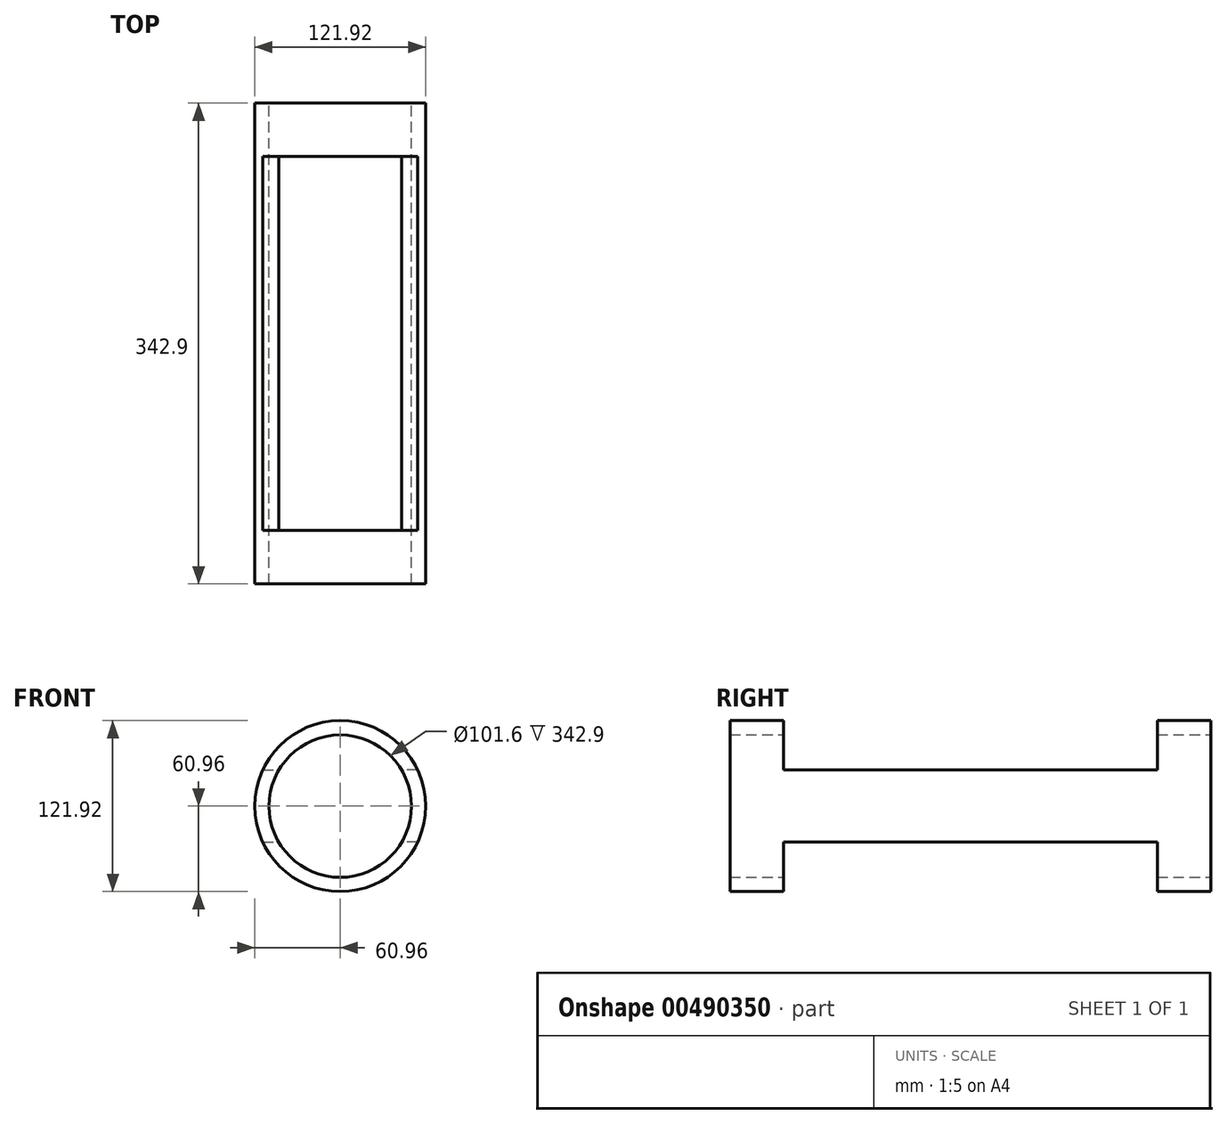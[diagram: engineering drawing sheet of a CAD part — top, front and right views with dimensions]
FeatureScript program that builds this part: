
annotation { "Feature Type Name" : "Feature", "Feature Type Description" : "" }
export const myFeature = defineFeature(function(context is Context, id is Id, definition is map)
    precondition{}
    {
        {
            var Q0;
            Q0=qCreatedBy(makeId("Front.planeOp"),FACE);
            var sketch = newSketch(context, id + "F0", { "sketchPlane" : qUnion([Q0])});
            skCircle(sketch, "E0", {"center": v(0, 0) * mm, "radius": 60.96 * mm});
            skCircle(sketch, "E1", {"center": v(0, 0) * mm, "radius": 50.8 * mm});
            skLineSegment(sketch, "E2", {"start": v(-55.27, -25.72) * mm, "end": v(-43.8, -25.72) * mm});
            skLineSegment(sketch, "E3", {"start": v(-55.27, 25.72) * mm, "end": v(-43.8, 25.72) * mm});
            skLineSegment(sketch, "E4", {"start": v(55.27, -25.72) * mm, "end": v(43.8, -25.72) * mm});
            skLineSegment(sketch, "E5", {"start": v(55.27, 25.72) * mm, "end": v(43.8, 25.72) * mm});
            skSolve(sketch);
        }
        {
            var Q0;
            {var subQ0=sQuery(id+"F0.wireOp",EDGE,"E2");Q0=makeQuery(id+"F0.imprint","IMPRINT",FACE,{"disambiguationData":[TD([[makeQuery(id+"F0.imprint","IMPRINT",EDGE,{"derivedFrom":subQ0}),1.0]])]});}
            var Q1;
            {var subQ0=sQuery(id+"F0.wireOp",EDGE,"E4");Q1=makeQuery(id+"F0.imprint","IMPRINT",FACE,{"disambiguationData":[TD([[makeQuery(id+"F0.imprint","IMPRINT",EDGE,{"derivedFrom":subQ0}),-1.0]])]});}
            extrude(context, id + "F1", {"entities" : qUnion([Q0, Q1]), "depth" : 304.8 * mm});
        }
        {
            var Q0;
            {var subQ0=sQuery(id+"F0.wireOp",EDGE,"E3");Q0=makeQuery(id+"F0.imprint","IMPRINT",FACE,{"disambiguationData":[TD([[makeQuery(id+"F0.imprint","IMPRINT",EDGE,{"derivedFrom":subQ0}),1.0]])]});}
            var Q1;
            {var subQ0=sQuery(id+"F0.wireOp",EDGE,"E2");Q1=makeQuery(id+"F0.imprint","IMPRINT",FACE,{"disambiguationData":[TD([[makeQuery(id+"F0.imprint","IMPRINT",EDGE,{"derivedFrom":subQ0}),-1.0]])]});}
            extrude(context, id + "F2", {"entities" : qUnion([Q0, Q1]), "operationType" : NewBodyOperationType.ADD, "depth" : 38.1 * mm});
        }
        {
            var Q0;
            Q0=makeQuery(id+"F1.opExtrude","CAP_FACE",FACE,{"disambiguationData":[OSD([sQuery(id+"F0.wireOp",EDGE,"E0"),sQuery(id+"F0.wireOp",EDGE,"E1"),sQuery(id+"F0.wireOp",EDGE,"E2"),sQuery(id+"F0.wireOp",EDGE,"E3")])],"isStart":false});
            var sketch = newSketch(context, id + "F3", { "sketchPlane" : qUnion([Q0])});
            skCircle(sketch, "E6", {"center": v(0, 0) * mm, "radius": 60.96 * mm});
            skCircle(sketch, "E7", {"center": v(0, 0) * mm, "radius": 50.8 * mm});
            skSolve(sketch);
        }
        {
            var Q0;
            {var subQ0=sQuery(id+"F3.wireOp",EDGE,"E6");var subQ1=makeQuery(id+"F1.opExtrude","CAP_EDGE",EDGE,{"disambiguationData":[OSD([sQuery(id+"F0.wireOp",EDGE,"E2")])],"isStart":false});var subQ2=makeQuery(id+"F3.imprint","INTERSECT",VERTEX,{"derivedFrom":[subQ1,subQ0]});Q0=makeQuery(id+"F3.imprint","IMPRINT",FACE,{"disambiguationData":[TD([[makeQuery(id+"F3.imprint","IMPRINT",EDGE,{"disambiguationData":[TD([[subQ2,-1.0]])],"derivedFrom":subQ0}),1.0]])]});}
            var Q1;
            {var subQ0=sQuery(id+"F3.wireOp",EDGE,"E6");var subQ1=makeQuery(id+"F1.opExtrude","CAP_EDGE",EDGE,{"disambiguationData":[OSD([sQuery(id+"F0.wireOp",EDGE,"E2")])],"isStart":false});var subQ2=makeQuery(id+"F3.imprint","INTERSECT",VERTEX,{"derivedFrom":[subQ1,subQ0]});Q1=makeQuery(id+"F3.imprint","IMPRINT",FACE,{"disambiguationData":[TD([[makeQuery(id+"F3.imprint","IMPRINT",EDGE,{"disambiguationData":[TD([[subQ2,1.0]])],"derivedFrom":subQ0}),1.0]])]});}
            extrude(context, id + "F4", {"entities" : qUnion([Q0, Q1]), "operationType" : NewBodyOperationType.ADD, "depth" : 38.1 * mm});
        }
    });
